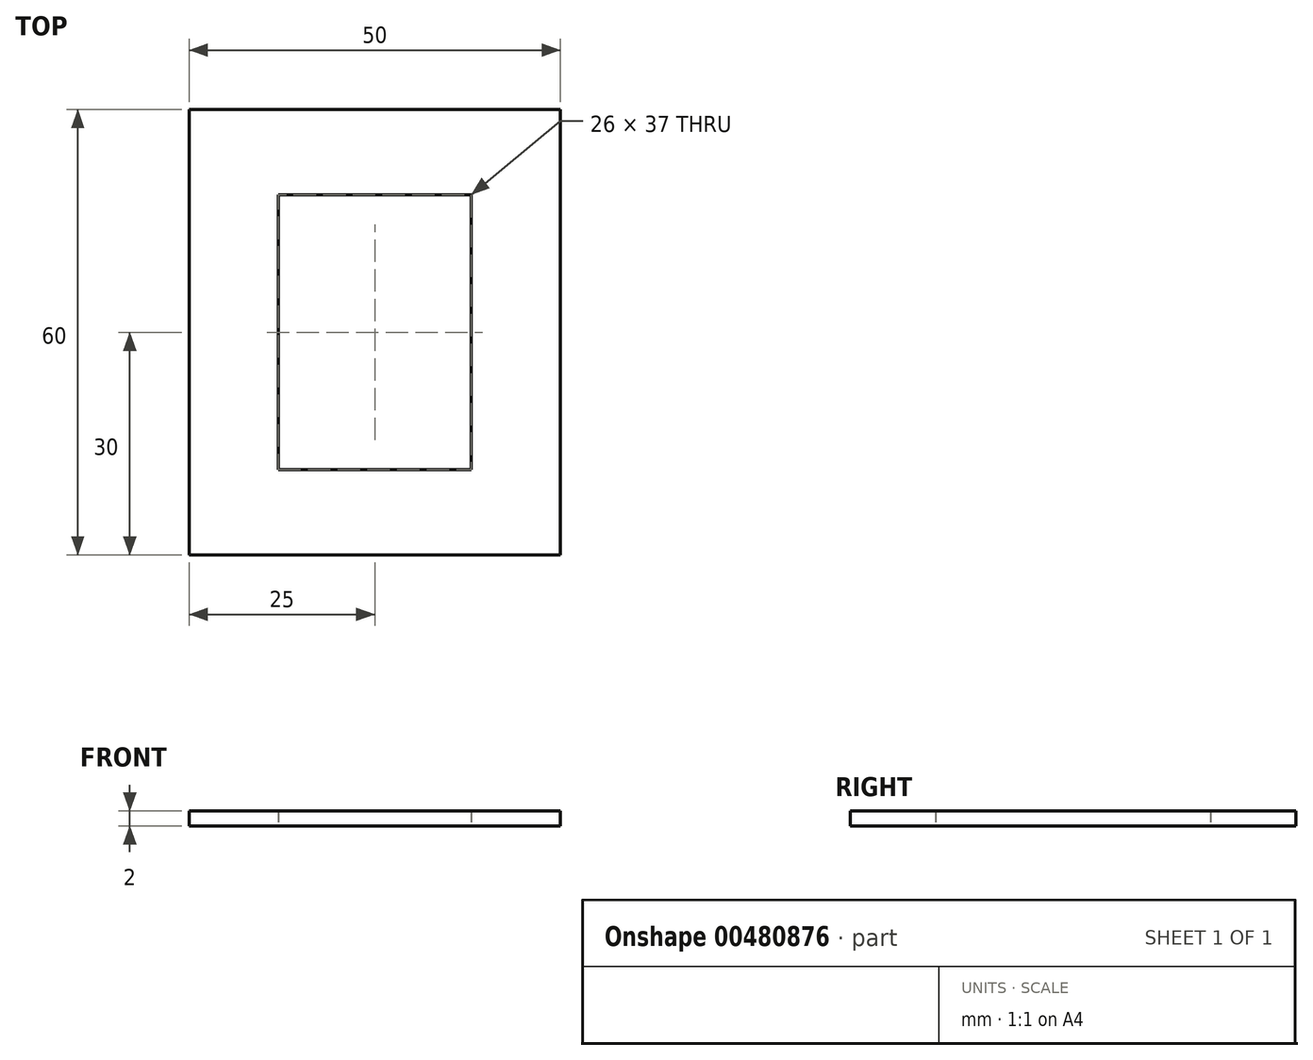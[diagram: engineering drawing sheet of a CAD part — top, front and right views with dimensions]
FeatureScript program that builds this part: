
annotation { "Feature Type Name" : "Feature", "Feature Type Description" : "" }
export const myFeature = defineFeature(function(context is Context, id is Id, definition is map)
    precondition{}
    {
        {
            var Q0;
            Q0=qCreatedBy(makeId("Top.planeOp"),FACE);
            var sketch = newSketch(context, id + "F0", { "sketchPlane" : qUnion([Q0])});
            skLineSegment(sketch, "E0.bottom", {"start": v(25, 30) * mm, "end": v(-25, 30) * mm});
            skLineSegment(sketch, "E0.top", {"start": v(25, -30) * mm, "end": v(-25, -30) * mm});
            skLineSegment(sketch, "E0.left", {"start": v(25, 30) * mm, "end": v(25, -30) * mm});
            skLineSegment(sketch, "E0.right", {"start": v(-25, 30) * mm, "end": v(-25, -30) * mm});
            skPoint(sketch, "E0.middle", {"position": v(0, 0) * mm});
            skSolve(sketch);
        }
        {
            var Q0;
            Q0=makeQuery(id+"F0.imprint","IMPRINT",FACE,{"disambiguationData":[TD([[makeQuery(id+"F0.imprint","IMPRINT",EDGE,{"derivedFrom":sQuery(id+"F0.wireOp",EDGE,"E0.bottom")}),1.0]])]});
            extrude(context, id + "F1", {"entities" : qUnion([Q0]), "depth" : 2 * mm});
        }
        {
            var Q0;
            Q0=makeQuery(id+"F1.opExtrude","CAP_FACE",FACE,{"disambiguationData":[OSD([sQuery(id+"F0.wireOp",EDGE,"E0.bottom"),sQuery(id+"F0.wireOp",EDGE,"E0.top"),sQuery(id+"F0.wireOp",EDGE,"E0.left"),sQuery(id+"F0.wireOp",EDGE,"E0.right")])],"isStart":true});
            var sketch = newSketch(context, id + "F2", { "sketchPlane" : qUnion([Q0])});
            skLineSegment(sketch, "E1.bottom", {"start": v(13, -18.5) * mm, "end": v(-13, -18.5) * mm});
            skLineSegment(sketch, "E1.top", {"start": v(13, 18.5) * mm, "end": v(-13, 18.5) * mm});
            skLineSegment(sketch, "E1.left", {"start": v(13, -18.5) * mm, "end": v(13, 18.5) * mm});
            skLineSegment(sketch, "E1.right", {"start": v(-13, -18.5) * mm, "end": v(-13, 18.5) * mm});
            skPoint(sketch, "E1.middle", {"position": v(0, 0) * mm});
            skSolve(sketch);
        }
        {
            var Q0;
            Q0=makeQuery(id+"F2.imprint","IMPRINT",FACE,{"disambiguationData":[TD([[makeQuery(id+"F2.imprint","IMPRINT",EDGE,{"derivedFrom":sQuery(id+"F2.wireOp",EDGE,"E1.bottom")}),-1.0]])]});
            extrude(context, id + "F3", {"entities" : qUnion([Q0]), "operationType" : NewBodyOperationType.REMOVE, "oppositeDirection" : true, "depth" : 25.4 * mm});
        }
    });
